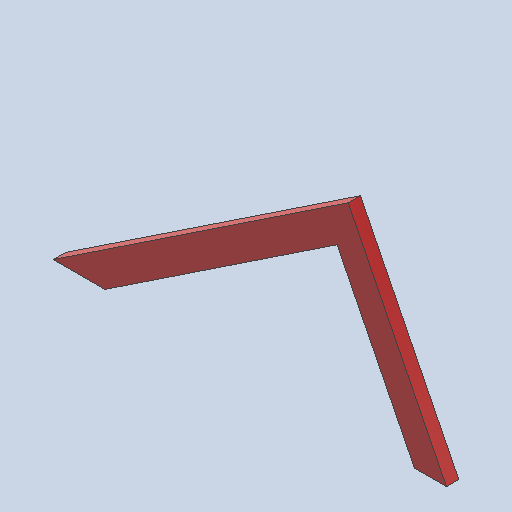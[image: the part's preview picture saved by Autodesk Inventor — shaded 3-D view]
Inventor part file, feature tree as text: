
AUTODESK INVENTOR PART (.ipt)
format: ipt  version: 2025.1 (Build 291241020, 241B)  size: 250,368 bytes
history: native  units: in
note: dims shown in document units (in); Inventor stores cm internally (conversion verified against a paired STEP export)
features: other x4, extrude x1, sketch x1, reference x1
ambient origin geometry x8: Origin, YZ Plane, XZ Plane, XY Plane, X Axis, Y Axis, Z Axis, Center Point
bodies: Solid1 (feature_tree)
feature tree (7):
  extrude  "Extrusion1"  Depth=1.5in TaperAngle=0.0deg
  sketch  "Sketch1"  dims[d2=3.5in d3=3.5in d4=1.5in d5=0.0in]
  reference  "Reference1"
  other  "<userpath>\Documents\Tburn24\B_Legs1\B_Legs0.iam"
  other  "B_Legs0.iam"
  other  "8'x2x4:4"
  other  "Finish1"
